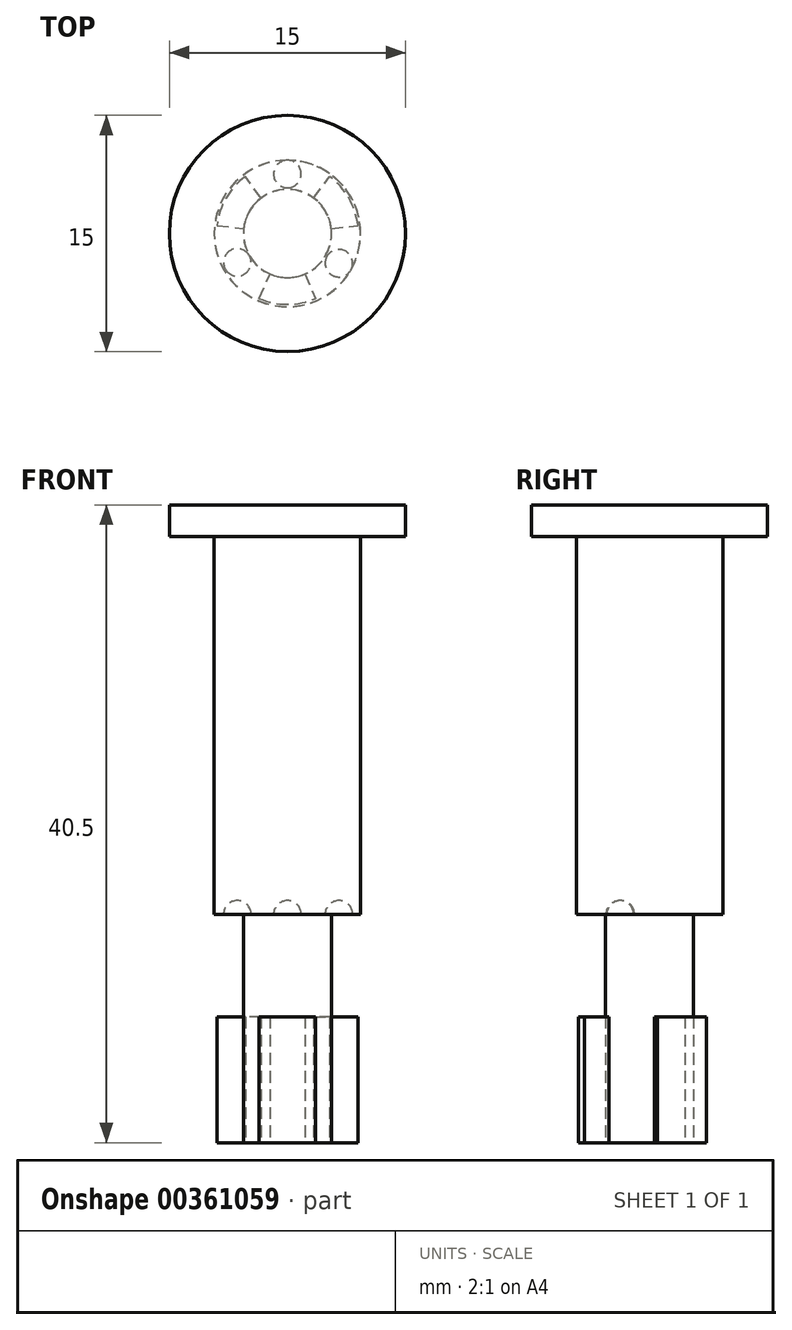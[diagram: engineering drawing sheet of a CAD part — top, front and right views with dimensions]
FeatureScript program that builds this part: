
annotation { "Feature Type Name" : "Feature", "Feature Type Description" : "" }
export const myFeature = defineFeature(function(context is Context, id is Id, definition is map)
    precondition{}
    {
        {
            var Q0;
            Q0=qCreatedBy(makeId("Top.planeOp"),FACE);
            var sketch = newSketch(context, id + "F0", { "sketchPlane" : qUnion([Q0])});
            skArc(sketch, "E0", {"start": v(-2.68, 3.62) * mm, "mid": v(-3.9, 2.25) * mm, "end": v(-4.47, 0.5) * mm});
            skCircle(sketch, "E1.0", {"center": v(0, 0) * mm, "radius": 2.8 * mm});
            skLineSegment(sketch, "E2", {"start": v(1.67, 2.25) * mm, "end": v(2.68, 3.62) * mm});
            skLineSegment(sketch, "E3", {"start": v(-1.67, 2.25) * mm, "end": v(-2.68, 3.62) * mm});
            skLineSegment(sketch, "E4.1.1", {"start": v(-1.12, -2.57) * mm, "end": v(-1.8, -4.13) * mm, "construction": true});
            skLineSegment(sketch, "E4.1.2", {"start": v(-2.78, 0.32) * mm, "end": v(-4.47, 0.5) * mm, "construction": true});
            skLineSegment(sketch, "E4.2.1", {"start": v(2.78, 0.32) * mm, "end": v(4.47, 0.5) * mm, "construction": true});
            skLineSegment(sketch, "E4.2.2", {"start": v(1.12, -2.57) * mm, "end": v(1.8, -4.13) * mm, "construction": true});
            skLineSegment(sketch, "E5", {"start": v(-1.8, -4.13) * mm, "end": v(-1.12, -2.57) * mm});
            skLineSegment(sketch, "E6", {"start": v(-4.47, 0.5) * mm, "end": v(-2.78, 0.32) * mm});
            skLineSegment(sketch, "E7", {"start": v(1.12, -2.57) * mm, "end": v(1.8, -4.13) * mm});
            skLineSegment(sketch, "E8", {"start": v(2.78, 0.32) * mm, "end": v(4.47, 0.5) * mm});
            skArc(sketch, "E9.trimOffspring", {"start": v(-1.8, -4.13) * mm, "mid": v(0, -4.5) * mm, "end": v(1.8, -4.13) * mm});
            skArc(sketch, "E10.trimOffspring", {"start": v(4.47, 0.5) * mm, "mid": v(3.9, 2.25) * mm, "end": v(2.68, 3.62) * mm});
            skSolve(sketch);
        }
        {
            var Q0;
            {var subQ0=sQuery(id+"F0.wireOp",EDGE,"E3");Q0=makeQuery(id+"F0.imprint","IMPRINT",FACE,{"disambiguationData":[TD([[makeQuery(id+"F0.imprint","IMPRINT",EDGE,{"derivedFrom":subQ0}),1.0]])]});}
            var Q1;
            {var subQ0=sQuery(id+"F0.wireOp",EDGE,"E2");Q1=makeQuery(id+"F0.imprint","IMPRINT",FACE,{"disambiguationData":[TD([[makeQuery(id+"F0.imprint","IMPRINT",EDGE,{"derivedFrom":subQ0}),-1.0]])]});}
            var Q2;
            {var subQ0=sQuery(id+"F0.wireOp",EDGE,"E5");Q2=makeQuery(id+"F0.imprint","IMPRINT",FACE,{"disambiguationData":[TD([[makeQuery(id+"F0.imprint","IMPRINT",EDGE,{"derivedFrom":subQ0}),-1.0]])]});}
            extrude(context, id + "F1", {"entities" : qUnion([Q0, Q1, Q2]), "depth" : 8 * mm});
        }
        {
            var Q0;
            {var subQ0=sQuery(id+"F0.wireOp",EDGE,"E1.0");var subQ4=makeQuery(id+"F0.imprint","INTERSECT",VERTEX,{"derivedFrom":[subQ0,sQuery(id+"F0.wireOp",EDGE,"E2")]});Q0=makeQuery(id+"F0.imprint","IMPRINT",FACE,{"disambiguationData":[TD([[makeQuery(id+"F0.imprint","IMPRINT",EDGE,{"disambiguationData":[TD([[subQ4,1.0]])],"derivedFrom":subQ0}),1.0]])]});}
            extrude(context, id + "F2", {"entities" : qUnion([Q0]), "depth" : (8 + 6.5) * mm});
        }
        {
            var Q0;
            Q0=makeQuery(id+"F2.opExtrude","CAP_FACE",FACE,{"disambiguationData":[OSD([sQuery(id+"F0.wireOp",EDGE,"E1.0")])],"isStart":false});
            var sketch = newSketch(context, id + "F3", { "sketchPlane" : qUnion([Q0])});
            skCircle(sketch, "E11", {"center": v(0, 0) * mm, "radius": 4.65 * mm});
            skSolve(sketch);
        }
        {
            var Q0;
            Q0=makeQuery(id+"F3.imprint","IMPRINT",FACE,{"disambiguationData":[TD([[makeQuery(id+"F3.imprint","IMPRINT",EDGE,{"derivedFrom":sQuery(id+"F3.wireOp",EDGE,"E11")}),1.0]])]});
            var Q1;
            Q1=makeQuery(id+"F3.imprint","IMPRINT",FACE,{"disambiguationData":[TD([[makeQuery(id+"F3.imprint","IMPRINT",EDGE,{"derivedFrom":makeQuery(id+"F2.opExtrude","CAP_EDGE",EDGE,{"disambiguationData":[OSD([sQuery(id+"F0.wireOp",EDGE,"E1.0")])],"isStart":false})}),1.0]])]});
            extrude(context, id + "F4", {"entities" : qUnion([Q0, Q1]), "operationType" : NewBodyOperationType.ADD, "depth" : 24 * mm, "offsetDistance" : 25 * mm});
        }
        {
            var Q0;
            Q0=makeQuery(id+"F4.opExtrude","CAP_FACE",FACE,{"disambiguationData":[OSD([sQuery(id+"F3.wireOp",EDGE,"E11")])],"isStart":false});
            var sketch = newSketch(context, id + "F5", { "sketchPlane" : qUnion([Q0])});
            skCircle(sketch, "E12", {"center": v(0, 0) * mm, "radius": 7.5 * mm});
            skSolve(sketch);
        }
        {
            var Q0;
            Q0=makeQuery(id+"F5.imprint","IMPRINT",FACE,{"disambiguationData":[TD([[makeQuery(id+"F5.imprint","IMPRINT",EDGE,{"derivedFrom":sQuery(id+"F5.wireOp",EDGE,"E12")}),1.0]])]});
            var Q1;
            Q1=makeQuery(id+"F5.imprint","IMPRINT",FACE,{"disambiguationData":[TD([[makeQuery(id+"F5.imprint","IMPRINT",EDGE,{"derivedFrom":makeQuery(id+"F4.opExtrude","CAP_EDGE",EDGE,{"disambiguationData":[OSD([sQuery(id+"F3.wireOp",EDGE,"E11")])],"isStart":false})}),1.0]])]});
            extrude(context, id + "F6", {"entities" : qUnion([Q0, Q1]), "operationType" : NewBodyOperationType.ADD, "depth" : 2 * mm, "offsetDistance" : 25 * mm});
        }
        {
            var Q0;
            Q0=makeQuery(id+"F4.opExtrude","CAP_FACE",FACE,{"disambiguationData":[OSD([sQuery(id+"F3.wireOp",EDGE,"E11")])],"isStart":true});
            var sketch = newSketch(context, id + "F7", { "sketchPlane" : qUnion([Q0])});
            skLineSegment(sketch, "E13", {"start": v(0, 0) * mm, "end": v(0, -4.65) * mm, "construction": true});
            skLineSegment(sketch, "E14", {"start": v(-2.42, 1.4) * mm, "end": v(-3.94, 2.27) * mm, "construction": true});
            skLineSegment(sketch, "E15", {"start": v(2.42, 1.4) * mm, "end": v(4.03, 2.32) * mm, "construction": true});
            skCircle(sketch, "E16", {"center": v(0, 0) * mm, "radius": 3.78 * mm, "construction": true});
            skPoint(sketch, "E17", {"position": v(-3.18, 1.84) * mm});
            skPoint(sketch, "E18", {"position": v(0, -3.78) * mm});
            skPoint(sketch, "E19", {"position": v(3.23, 1.86) * mm});
            skArc(sketch, "E20", {"start": v(-3.94, 2.27) * mm, "mid": v(-3.62, 1.08) * mm, "end": v(-2.42, 1.4) * mm});
            skArc(sketch, "E21", {"start": v(4.03, 2.32) * mm, "mid": v(2.83, 2.65) * mm, "end": v(2.51, 1.45) * mm});
            skPoint(sketch, "E22", {"position": v(0, -2.9) * mm});
            skArc(sketch, "E23", {"start": v(0, -4.65) * mm, "mid": v(0.88, -3.78) * mm, "end": v(0, -2.9) * mm});
            skLineSegment(sketch, "E24", {"start": v(-3.94, 2.27) * mm, "end": v(-2.42, 1.4) * mm});
            skLineSegment(sketch, "E25", {"start": v(2.42, 1.4) * mm, "end": v(4.03, 2.32) * mm});
            skLineSegment(sketch, "E26", {"start": v(0, -2.9) * mm, "end": v(0, -4.65) * mm});
            skSolve(sketch);
        }
        {
            var Q0;
            Q0=makeQuery(id+"F7.imprint","IMPRINT",FACE,{"disambiguationData":[TD([[makeQuery(id+"F7.imprint","IMPRINT",EDGE,{"derivedFrom":sQuery(id+"F7.wireOp",EDGE,"E20")}),1.0]])]});
            var Q1;
            Q1=sQuery(id+"F7.wireOp",EDGE,"E24");
            revolve(context, id + "F8", {"operationType" : NewBodyOperationType.REMOVE, "entities" : qUnion([Q0]), "axis" : qUnion([Q1]), "revolveType" : RevolveType.FULL});
        }
        {
            var Q0;
            Q0=makeQuery(id+"F7.imprint","IMPRINT",FACE,{"disambiguationData":[TD([[makeQuery(id+"F7.imprint","IMPRINT",EDGE,{"derivedFrom":sQuery(id+"F7.wireOp",EDGE,"E21")}),1.0]])]});
            var Q1;
            Q1=sQuery(id+"F7.wireOp",EDGE,"E25");
            revolve(context, id + "F9", {"operationType" : NewBodyOperationType.REMOVE, "entities" : qUnion([Q0]), "axis" : qUnion([Q1]), "revolveType" : RevolveType.FULL, "oppositeDirection" : true});
        }
        {
            var Q0;
            Q0=makeQuery(id+"F7.imprint","IMPRINT",FACE,{"disambiguationData":[TD([[makeQuery(id+"F7.imprint","IMPRINT",EDGE,{"derivedFrom":sQuery(id+"F7.wireOp",EDGE,"E23")}),1.0]])]});
            var Q1;
            Q1=sQuery(id+"F7.wireOp",EDGE,"E26");
            revolve(context, id + "F10", {"operationType" : NewBodyOperationType.REMOVE, "entities" : qUnion([Q0]), "axis" : qUnion([Q1]), "revolveType" : RevolveType.FULL, "oppositeDirection" : true});
        }
    });
